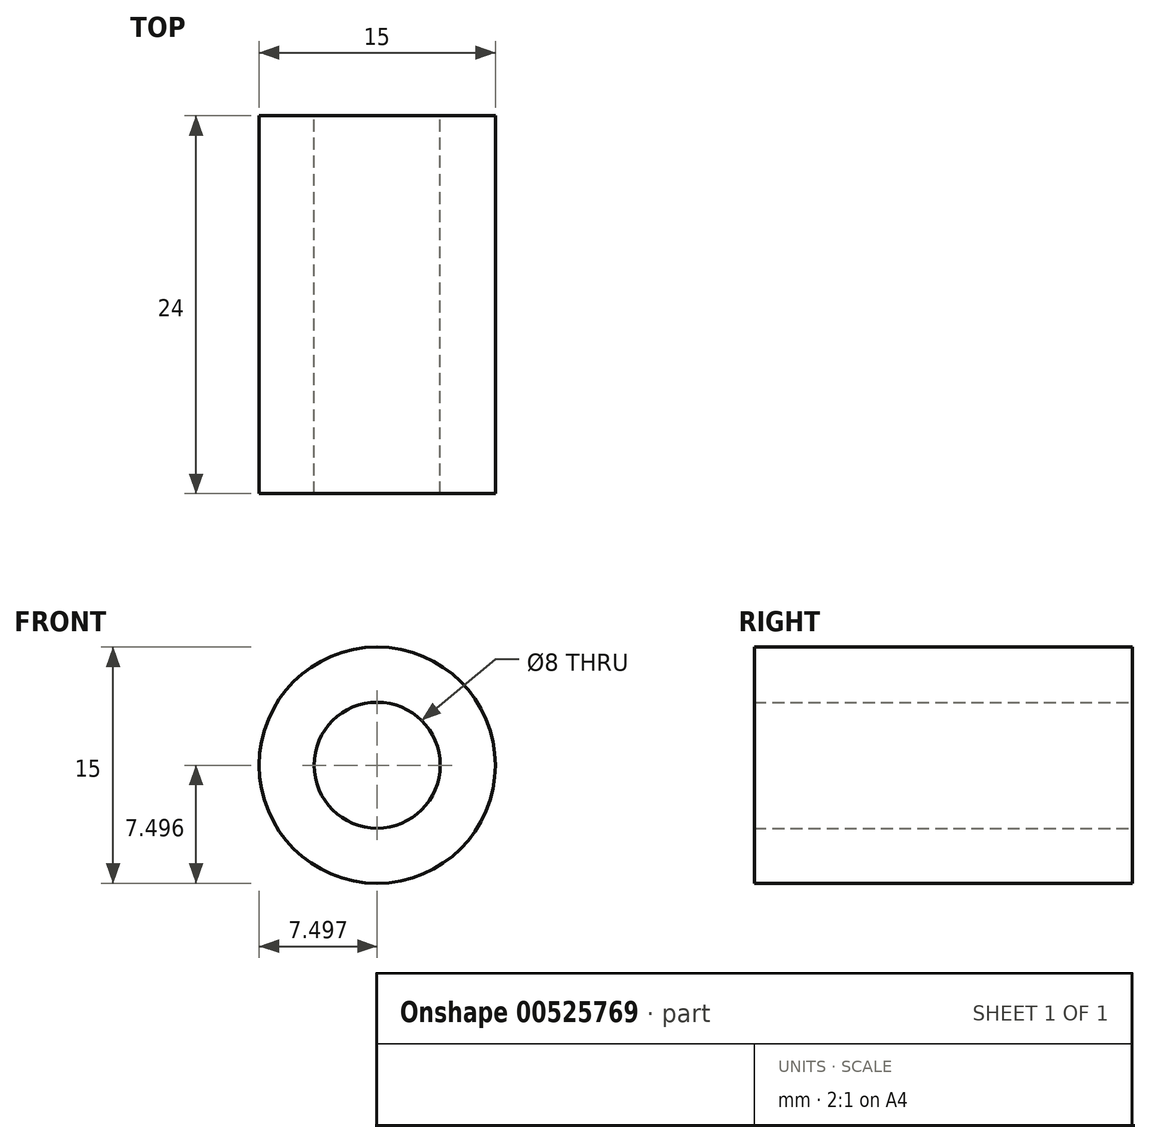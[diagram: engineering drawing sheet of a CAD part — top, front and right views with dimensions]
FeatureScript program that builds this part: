
annotation { "Feature Type Name" : "Feature", "Feature Type Description" : "" }
export const myFeature = defineFeature(function(context is Context, id is Id, definition is map)
    precondition{}
    {
        {
            var Q0;
            Q0=qCreatedBy(makeId("Front.planeOp"),FACE);
            var sketch = newSketch(context, id + "F0", { "sketchPlane" : qUnion([Q0])});
            skCircle(sketch, "E0", {"center": v(15.62, 19.83) * mm, "radius": 4 * mm});
            skCircle(sketch, "E1", {"center": v(15.62, 19.83) * mm, "radius": 7.5 * mm});
            skSolve(sketch);
        }
        {
            var Q0;
            Q0=makeQuery(id+"F0.imprint","IMPRINT",FACE,{"disambiguationData":[TD([[makeQuery(id+"F0.imprint","IMPRINT",EDGE,{"derivedFrom":sQuery(id+"F0.wireOp",EDGE,"E0")}),-1.0]])]});
            extrude(context, id + "F1", {"entities" : qUnion([Q0]), "depth" : 24 * mm, "offsetDistance" : 25 * mm});
        }
    });
